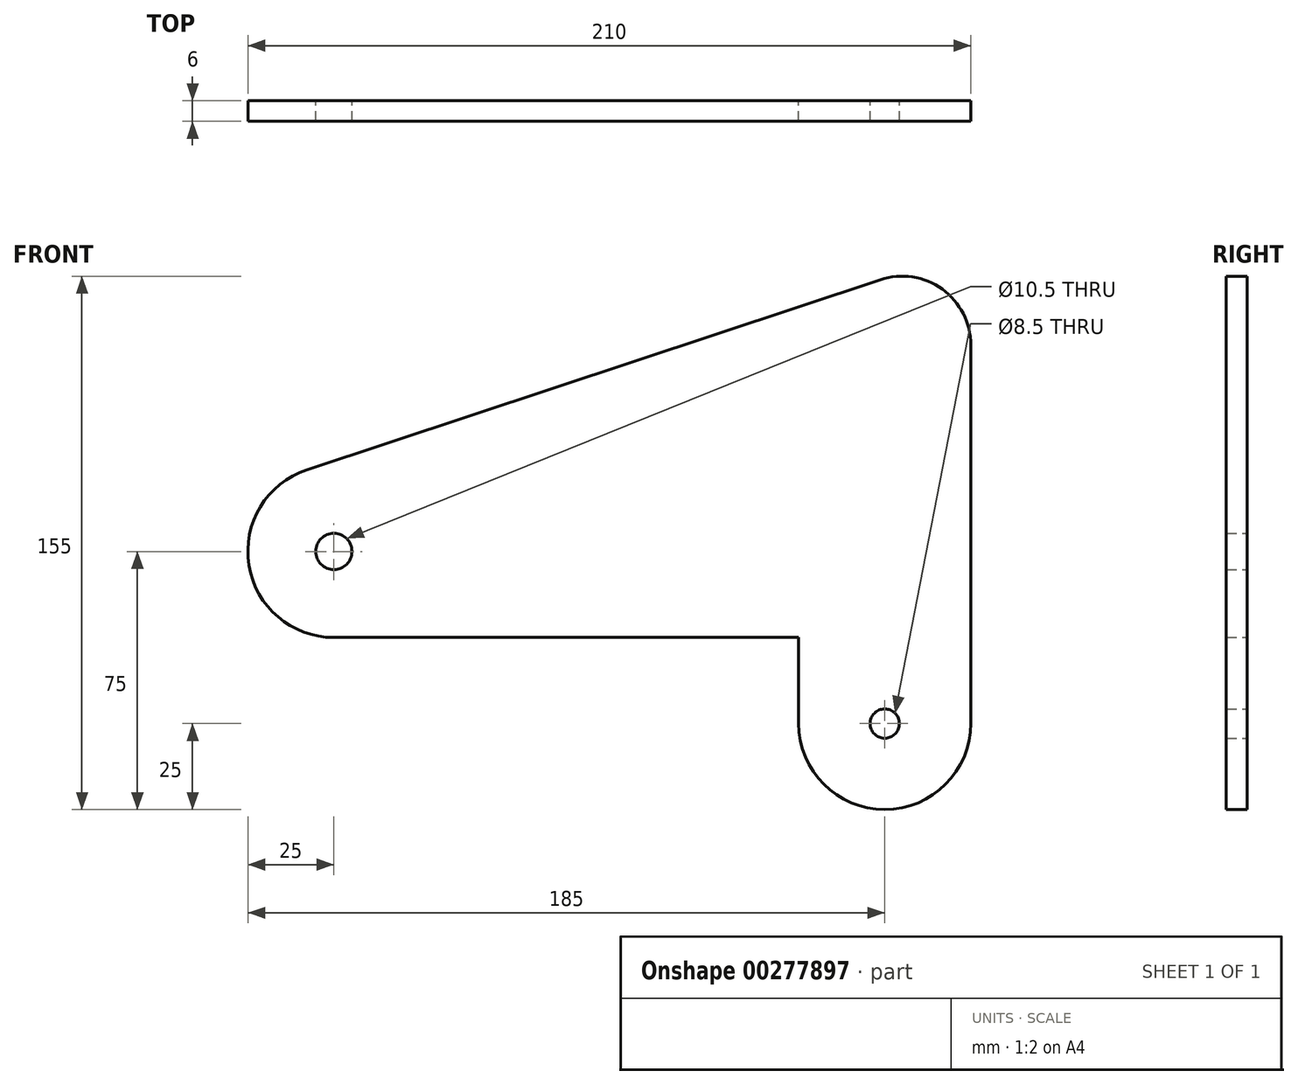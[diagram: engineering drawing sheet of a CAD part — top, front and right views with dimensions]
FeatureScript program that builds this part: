
annotation { "Feature Type Name" : "Feature", "Feature Type Description" : "" }
export const myFeature = defineFeature(function(context is Context, id is Id, definition is map)
    precondition{}
    {
        {
            var Q0;
            Q0=qCreatedBy(makeId("Front.planeOp"),FACE);
            var sketch = newSketch(context, id + "F0", { "sketchPlane" : qUnion([Q0])});
            skArc(sketch, "E0", {"start": v(-25, 0) * mm, "mid": v(0, -25) * mm, "end": v(25, 0) * mm});
            skLineSegment(sketch, "E1", {"start": v(-25, 0) * mm, "end": v(-25, 25) * mm});
            skArc(sketch, "E2", {"start": v(-167.87, 73.73) * mm, "mid": v(-184.68, 46.01) * mm, "end": v(-160, 25) * mm});
            skArc(sketch, "E3", {"start": v(25, 110) * mm, "mid": v(16.7, 126.22) * mm, "end": v(-1.3, 128.98) * mm});
            skLineSegment(sketch, "E4", {"start": v(-25, 25) * mm, "end": v(-160, 25) * mm});
            skLineSegment(sketch, "E5", {"start": v(-167.87, 73.73) * mm, "end": v(-1.3, 128.98) * mm});
            skLineSegment(sketch, "E6", {"start": v(25, 0) * mm, "end": v(25, 110) * mm});
            skCircle(sketch, "E7", {"center": v(-160, 50) * mm, "radius": 5.25 * mm});
            skCircle(sketch, "E8", {"center": v(0, 0) * mm, "radius": 4.25 * mm});
            skSolve(sketch);
        }
        {
            var Q0;
            Q0=makeQuery(id+"F0.imprint","IMPRINT",FACE,{"disambiguationData":[TD([[makeQuery(id+"F0.imprint","IMPRINT",EDGE,{"derivedFrom":sQuery(id+"F0.wireOp",EDGE,"E0")}),1.0]])]});
            extrude(context, id + "F1", {"entities" : qUnion([Q0]), "depth" : 6 * mm});
        }
    });
